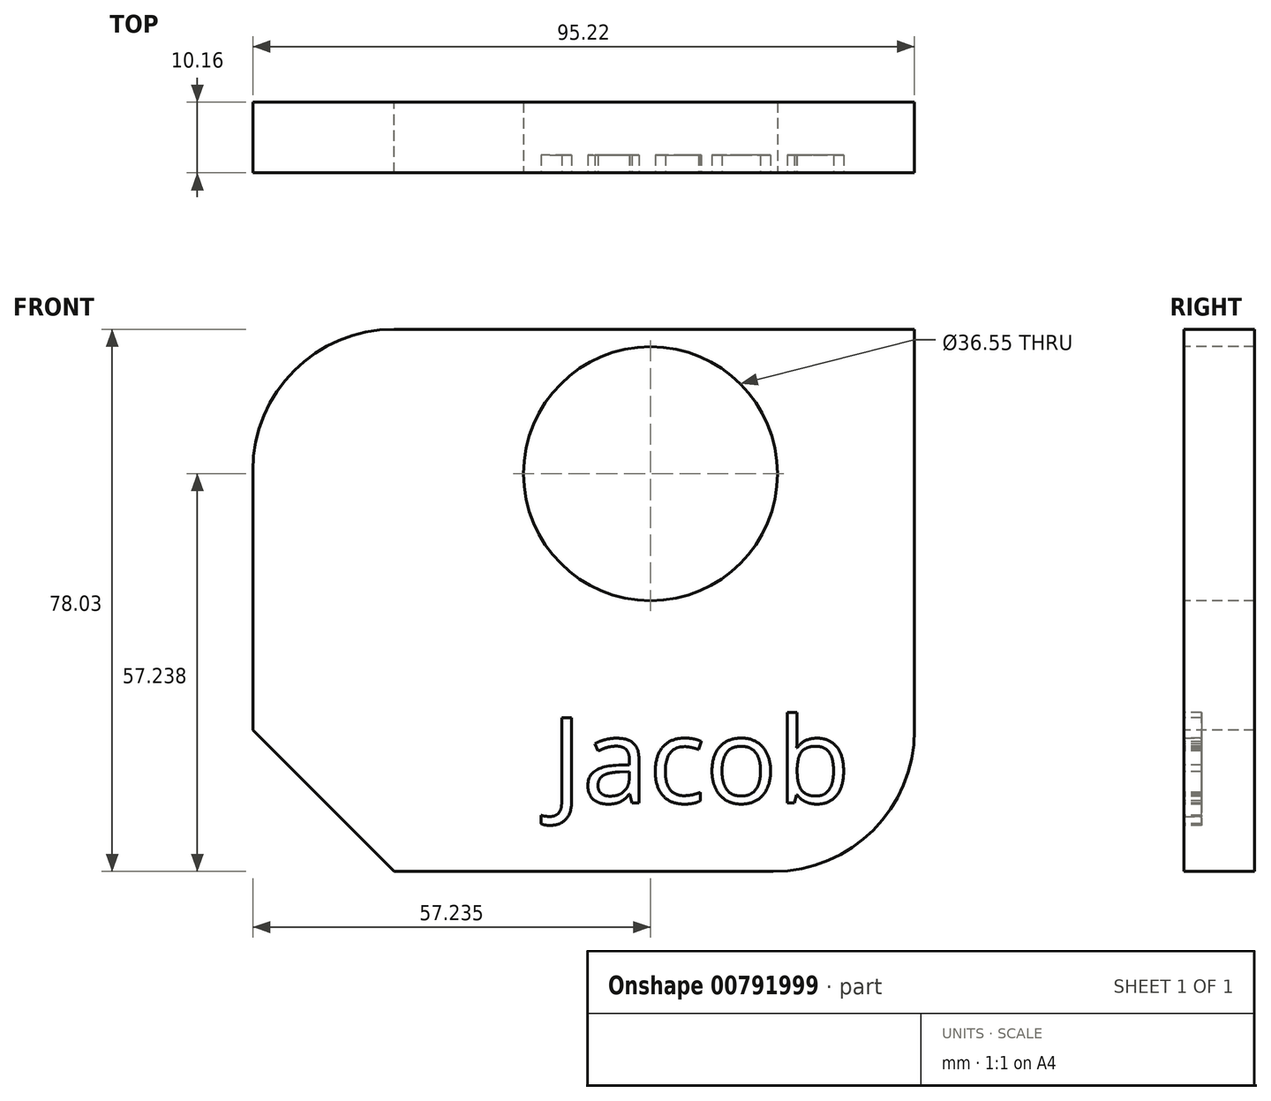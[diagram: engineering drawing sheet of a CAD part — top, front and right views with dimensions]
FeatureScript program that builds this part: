
annotation { "Feature Type Name" : "Feature", "Feature Type Description" : "" }
export const myFeature = defineFeature(function(context is Context, id is Id, definition is map)
    precondition{}
    {
        {
            var Q0;
            Q0=qCreatedBy(makeId("Front.planeOp"),FACE);
            var sketch = newSketch(context, id + "F0", { "sketchPlane" : qUnion([Q0])});
            skLineSegment(sketch, "E0.bottom", {"start": v(-45.1, 32.27) * mm, "end": v(50.12, 32.27) * mm});
            skLineSegment(sketch, "E0.top", {"start": v(-45.1, -45.76) * mm, "end": v(50.12, -45.76) * mm});
            skLineSegment(sketch, "E0.left", {"start": v(-45.1, 32.27) * mm, "end": v(-45.1, -45.76) * mm});
            skLineSegment(sketch, "E0.right", {"start": v(50.12, 32.27) * mm, "end": v(50.12, -45.76) * mm});
            skSolve(sketch);
        }
        {
            var Q0;
            Q0=makeQuery(id+"F0.imprint","IMPRINT",FACE,{"disambiguationData":[TD([[makeQuery(id+"F0.imprint","IMPRINT",EDGE,{"derivedFrom":sQuery(id+"F0.wireOp",EDGE,"E0.bottom")}),-1.0]])]});
            extrude(context, id + "F1", {"entities" : qUnion([Q0]), "depth" : 10.16 * mm, "offsetDistance" : 25.4 * mm});
        }
        {
            var Q0;
            Q0=makeQuery(id+"F1.opExtrude","CAP_FACE",FACE,{"disambiguationData":[OSD([sQuery(id+"F0.wireOp",EDGE,"E0.bottom"),sQuery(id+"F0.wireOp",EDGE,"E0.top"),sQuery(id+"F0.wireOp",EDGE,"E0.left"),sQuery(id+"F0.wireOp",EDGE,"E0.right")])],"isStart":false});
            var sketch = newSketch(context, id + "F2", { "sketchPlane" : qUnion([Q0])});
            skCircle(sketch, "E1", {"center": v(12.14, 11.48) * mm, "radius": 18.27 * mm});
            skSolve(sketch);
        }
        {
            var Q0;
            Q0=makeQuery(id+"F2.imprint","IMPRINT",FACE,{"disambiguationData":[TD([[makeQuery(id+"F2.imprint","IMPRINT",EDGE,{"derivedFrom":sQuery(id+"F2.wireOp",EDGE,"E1")}),1.0]])]});
            extrude(context, id + "F3", {"entities" : qUnion([Q0]), "operationType" : NewBodyOperationType.REMOVE, "oppositeDirection" : true, "depth" : 25.4 * mm, "offsetDistance" : 25.4 * mm});
        }
        {
            var Q0;
            Q0=makeQuery(id+"F1.opExtrude","SWEPT_EDGE",EDGE,{"disambiguationData":[OSD([sQuery(id+"F0.wireOp",EDGE,"E0.bottom"),sQuery(id+"F0.wireOp",EDGE,"E0.left")])]});
            fillet(context, id + "F4", {"entities" : qUnion([Q0]), "radius" : 20.32 * mm, "tangentPropagation" : true, "allowEdgeOverflow" : false});
        }
        {
            var Q0;
            Q0=makeQuery(id+"F1.opExtrude","SWEPT_EDGE",EDGE,{"disambiguationData":[OSD([sQuery(id+"F0.wireOp",EDGE,"E0.top"),sQuery(id+"F0.wireOp",EDGE,"E0.right")])]});
            fillet(context, id + "F5", {"entities" : qUnion([Q0]), "radius" : 20.32 * mm, "tangentPropagation" : true, "allowEdgeOverflow" : false});
        }
        {
            var Q0;
            Q0=makeQuery(id+"F1.opExtrude","SWEPT_EDGE",EDGE,{"disambiguationData":[OSD([sQuery(id+"F0.wireOp",EDGE,"E0.top"),sQuery(id+"F0.wireOp",EDGE,"E0.left")])]});
            chamfer(context, id + "F6", {"entities" : qUnion([Q0]), "width" : 20.32 * mm, "tangentPropagation" : true});
        }
        {
            var Q0;
            Q0=makeQuery(id+"F1.opExtrude","CAP_FACE",FACE,{"disambiguationData":[OSD([sQuery(id+"F0.wireOp",EDGE,"E0.bottom"),sQuery(id+"F0.wireOp",EDGE,"E0.top"),sQuery(id+"F0.wireOp",EDGE,"E0.left"),sQuery(id+"F0.wireOp",EDGE,"E0.right")])],"isStart":false});
            var sketch = newSketch(context, id + "F7", { "sketchPlane" : qUnion([Q0])});
            skText(sketch, "E2", { "text": "Jacob", "fontName": "OpenSans-Regular.ttf"});
            const initialGuessF7  = {"E2": [-0.00225, -0.0359, 1, 0, 0.01234]};
            skSetInitialGuess(sketch, initialGuessF7);
            skSolve(sketch);
        }
        {
            var Q0;
            Q0 = qSketchRegion(id + "F7", true);
            extrude(context, id + "F8", {"entities" : qUnion([Q0]), "operationType" : NewBodyOperationType.REMOVE, "oppositeDirection" : true, "depth" : 2.54 * mm, "offsetDistance" : 25.4 * mm});
        }
    });
